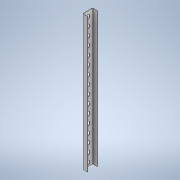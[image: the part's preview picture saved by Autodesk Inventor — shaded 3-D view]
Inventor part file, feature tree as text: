
AUTODESK INVENTOR PART (.ipt)
format: ipt  version: 2022 (Build 260153000, 153)  size: 239,616 bytes
history: native  units: mm
features: sketch x5, other x4, projected_geometry x4, sheet_metal_op x3, extrude x2
ambient origin geometry x8: Origin, YZ Plane, XZ Plane, XY Plane, X Axis, Y Axis, Z Axis, Center Point
bodies: Solid1 (feature_tree)
feature tree (18):
  sheet_metal_op  "Contour Flange1"
  extrude  "Extrusion1"  Depth=15.0mm
  extrude  "Extrusion2"  Depth=1.5mm
  sketch  "Sketch1"  dims[d0=30.0mm d1=15.0mm]
  other  "Plate1"
  sheet_metal_op  "Bend1"
  sheet_metal_op  "Corner1"
  sketch  "Sketch2"  dims[d2=15.0mm d3=1.5mm]
  projected_geometry  "Projected Loop1"
  sketch  "Sketch5"  dims[d4=1.5mm]
  projected_geometry  "Projected Loop6"
  sketch  "Sketch6"  dims[d5=0.75mm]
  projected_geometry  "Projected Loop7"
  projected_geometry  "Projected Loop8"
  sketch  "Sketch7"  dims[d6=3.0mm d7=1.5mm d8=400.0mm d9=1.5mm d10=0.5mm d11=6.0mm d12=1.5mm d13=1.5mm d14=12.2mm d15=10.0mm d16=12.0mm d17=160.0mm d19=25.0mm d20=10.0mm d22=10.0mm d24=1.5mm d25=0.0mm d26=1.5mm d27=0.0mm d28=3.0mm d29=0.0mm d30=3.0mm d31=0.0mm d32=10.0mm]
  other  "Cut1"
  other  "Cut2"
  other  "Definition1"
